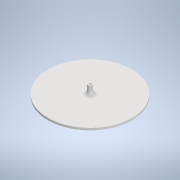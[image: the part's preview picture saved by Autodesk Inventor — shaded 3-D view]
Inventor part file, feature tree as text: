
AUTODESK INVENTOR PART (.ipt)
format: ipt  version: 2022 (Build 260153000, 153)  size: 113,664 bytes
history: native  units: mm
features: extrude x2, sketch x2, fillet x1
ambient origin geometry x8: Origin, YZ Plane, XZ Plane, XY Plane, X Axis, Y Axis, Z Axis, Center Point
bodies: Solid1 (feature_tree)
feature tree (5):
  extrude  "Extrusion1"  Depth=5.0mm TaperAngle=0.0deg
  extrude  "Extrusion2"  Depth=10.0mm
  fillet  "Fillet1"  Radius=20.0mm
  sketch  "Sketch1"  dims[d0=200.0mm d1=5.0mm d2=0.0mm]
  sketch  "Sketch2"  dims[d3=5.0mm d4=10.0mm d5=20.0mm d6=0.0mm d7=10.0mm]
